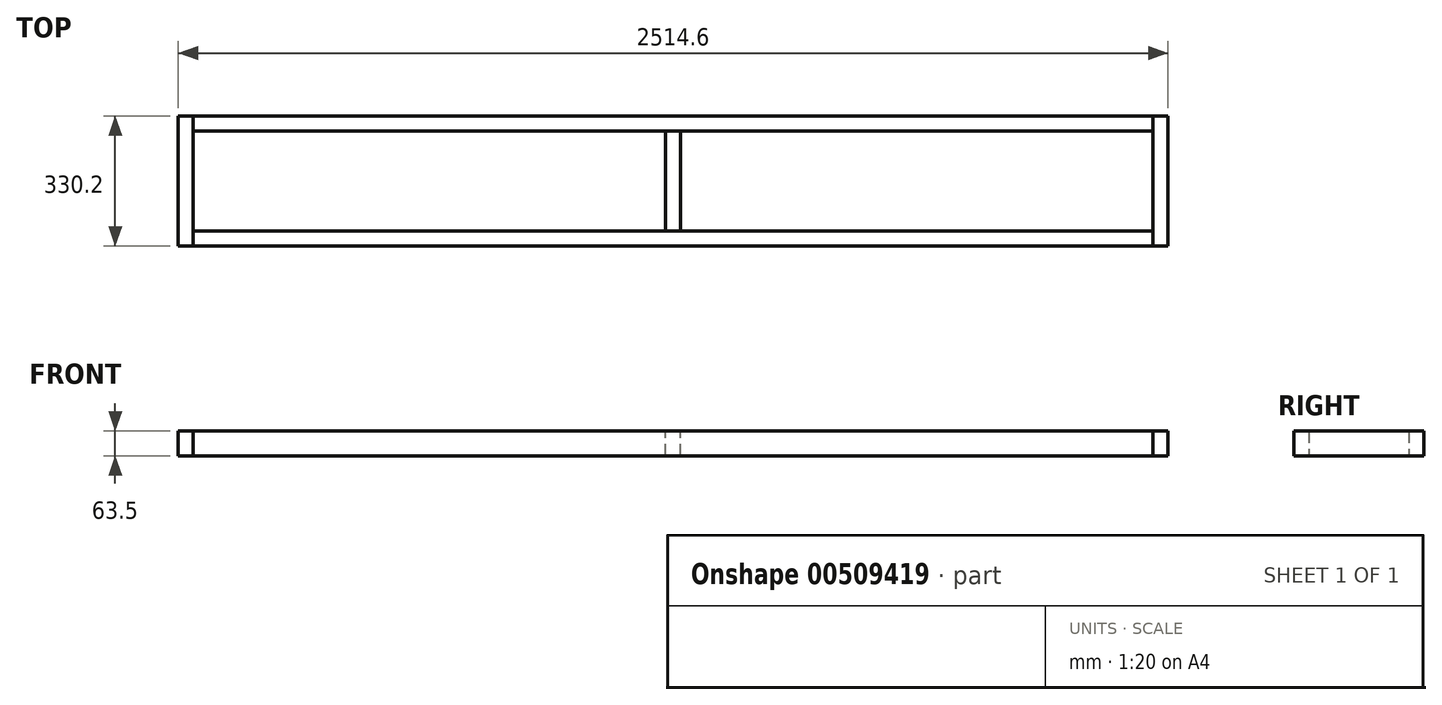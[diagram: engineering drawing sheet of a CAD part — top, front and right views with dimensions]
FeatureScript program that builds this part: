
annotation { "Feature Type Name" : "Feature", "Feature Type Description" : "" }
export const myFeature = defineFeature(function(context is Context, id is Id, definition is map)
    precondition{}
    {
        {
            var Q0;
            Q0=qCreatedBy(makeId("Right.planeOp"),FACE);
            var sketch = newSketch(context, id + "F0", { "sketchPlane" : qUnion([Q0])});
            skLineSegment(sketch, "E0.bottom", {"start": v(19.05, 31.75) * mm, "end": v(-19.05, 31.75) * mm});
            skLineSegment(sketch, "E0.top", {"start": v(19.05, -31.75) * mm, "end": v(-19.05, -31.75) * mm});
            skLineSegment(sketch, "E0.left", {"start": v(19.05, 31.75) * mm, "end": v(19.05, -31.75) * mm});
            skLineSegment(sketch, "E0.right", {"start": v(-19.05, 31.75) * mm, "end": v(-19.05, -31.75) * mm});
            skPoint(sketch, "E0.middle", {"position": v(0, 0) * mm});
            skSolve(sketch);
        }
        {
            var Q0;
            Q0=makeQuery(id+"F0.imprint","IMPRINT",FACE,{"disambiguationData":[TD([[makeQuery(id+"F0.imprint","IMPRINT",EDGE,{"derivedFrom":sQuery(id+"F0.wireOp",EDGE,"E0.bottom")}),1.0]])]});
            extrude(context, id + "F1", {"entities" : qUnion([Q0]), "depth" : 2438.4 * mm});
        }
        {
            var Q0;
            Q0=makeQuery(id+"F1.opExtrude","SWEPT_FACE",FACE,{"disambiguationData":[OSD([sQuery(id+"F0.wireOp",EDGE,"E0.right")])]});
            var sketch = newSketch(context, id + "F2", { "sketchPlane" : qUnion([Q0])});
            skLineSegment(sketch, "E1.bottom", {"start": v(0, 31.75) * mm, "end": v(-38.1, 31.75) * mm});
            skLineSegment(sketch, "E1.top", {"start": v(0, -31.75) * mm, "end": v(-38.1, -31.75) * mm});
            skLineSegment(sketch, "E1.left", {"start": v(0, 31.75) * mm, "end": v(0, -31.75) * mm});
            skLineSegment(sketch, "E1.right", {"start": v(-38.1, 31.75) * mm, "end": v(-38.1, -31.75) * mm});
            skSolve(sketch);
        }
        {
            var Q0;
            Q0=makeQuery(id+"F2.imprint","IMPRINT",FACE,{"disambiguationData":[TD([[makeQuery(id+"F2.imprint","IMPRINT",EDGE,{"derivedFrom":sQuery(id+"F2.wireOp",EDGE,"E1.bottom")}),1.0]])]});
            extrude(context, id + "F3", {"entities" : qUnion([Q0]), "oppositeDirection" : true, "depth" : 330.2 * mm});
        }
        {
            var Q0;
            Q0=makeQuery(id+"F1.opExtrude","SWEPT_BODY",BODY,{"disambiguationData":[OSD([sQuery(id+"F0.wireOp",EDGE,"E0.bottom"),sQuery(id+"F0.wireOp",EDGE,"E0.top"),sQuery(id+"F0.wireOp",EDGE,"E0.left"),sQuery(id+"F0.wireOp",EDGE,"E0.right")])]});
            transform(context, id + "F4", {"entities" : qUnion([Q0]), "transformType" : TransformType.TRANSLATION_3D, "dx" : 0 * mm, "dy" : 292.1 * mm, "dz" : 0 * mm, "makeCopy" : true});
        }
        {
            var Q0;
            Q0=makeQuery(id+"F3.opExtrude","SWEPT_BODY",BODY,{"disambiguationData":[OSD([sQuery(id+"F2.wireOp",EDGE,"E1.bottom"),sQuery(id+"F2.wireOp",EDGE,"E1.top"),sQuery(id+"F2.wireOp",EDGE,"E1.left"),sQuery(id+"F2.wireOp",EDGE,"E1.right")])]});
            transform(context, id + "F5", {"entities" : qUnion([Q0]), "transformType" : TransformType.TRANSLATION_3D, "dx" : 2476.5 * mm, "dy" : 0 * mm, "dz" : 0 * mm, "makeCopy" : true});
        }
        {
            var Q0;
            Q0=makeQuery(id+"F4.opPattern","COPY",FACE,{"derivedFrom":makeQuery(id+"F1.opExtrude","SWEPT_FACE",FACE,{"disambiguationData":[OSD([sQuery(id+"F0.wireOp",EDGE,"E0.right")])]}),"instanceName":"1"});
            var sketch = newSketch(context, id + "F6", { "sketchPlane" : qUnion([Q0])});
            skLineSegment(sketch, "E2", {"start": v(1219.2, 31.75) * mm, "end": v(1219.2, -31.75) * mm, "construction": true});
            skLineSegment(sketch, "E3.bottom", {"start": v(1238.25, 31.75) * mm, "end": v(1200.15, 31.75) * mm});
            skLineSegment(sketch, "E3.top", {"start": v(1238.25, -31.75) * mm, "end": v(1200.15, -31.75) * mm});
            skLineSegment(sketch, "E3.left", {"start": v(1238.25, 31.75) * mm, "end": v(1238.25, -31.75) * mm});
            skLineSegment(sketch, "E3.right", {"start": v(1200.15, 31.75) * mm, "end": v(1200.15, -31.75) * mm});
            skPoint(sketch, "E3.middle", {"position": v(1219.2, 0) * mm});
            skSolve(sketch);
        }
        {
            var Q0;
            Q0 = qSketchRegion(id + "F6", true);
            extrude(context, id + "F7", {"entities" : qUnion([Q0]), "endBound" : BoundingType.UP_TO_NEXT, "depth" : 25.4 * mm});
        }
    });
